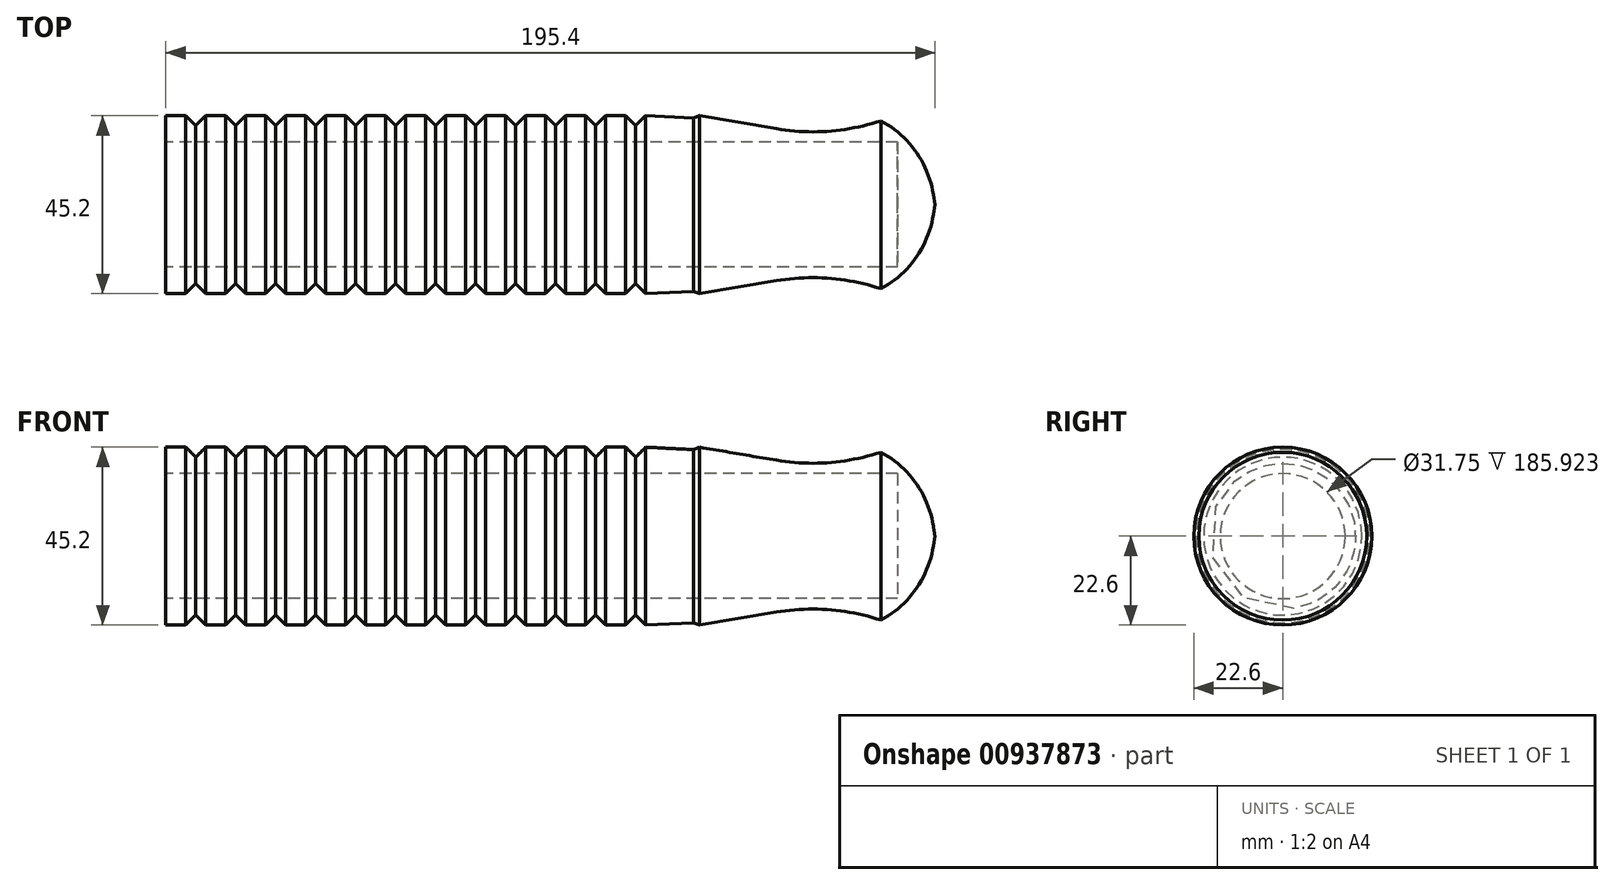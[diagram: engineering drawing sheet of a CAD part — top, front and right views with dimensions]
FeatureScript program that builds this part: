
annotation { "Feature Type Name" : "Feature", "Feature Type Description" : "" }
export const myFeature = defineFeature(function(context is Context, id is Id, definition is map)
    precondition{}
    {
        {
            var Q0;
            Q0=qCreatedBy(makeId("Top.planeOp"),FACE);
            var sketch = newSketch(context, id + "F0", { "sketchPlane" : qUnion([Q0])});
            skLineSegment(sketch, "E0", {"start": v(0, 0) * mm, "end": v(254, 0) * mm});
            skLineSegment(sketch, "E1", {"start": v(254, 0) * mm, "end": v(254, 25.4) * mm});
            skLineSegment(sketch, "E2", {"start": v(254, 25.4) * mm, "end": v(0, 25.4) * mm});
            skLineSegment(sketch, "E3", {"start": v(0, 25.4) * mm, "end": v(0, 0) * mm});
            skLineSegment(sketch, "E4", {"start": v(68.08, 0) * mm, "end": v(68.08, 22.6) * mm});
            skLineSegment(sketch, "E5", {"start": v(187.98, 22.6) * mm, "end": v(187.98, 0) * mm});
            skLineSegment(sketch, "E6", {"start": v(68.08, 22.6) * mm, "end": v(73.16, 22.6) * mm});
            skLineSegment(sketch, "E7", {"start": v(0, 0) * mm, "end": v(0, 15.88) * mm});
            skLineSegment(sketch, "E8", {"start": v(0, 15.88) * mm, "end": v(254, 15.88) * mm});
            skLineSegment(sketch, "E9", {"start": v(75.7, 20.06) * mm, "end": v(73.16, 22.6) * mm});
            skLineSegment(sketch, "E10", {"start": v(75.7, 20.06) * mm, "end": v(75.7, 22.6) * mm});
            skLineSegment(sketch, "E11.MirrorCS", {"start": v(75.7, 20.06) * mm, "end": v(78.24, 22.6) * mm});
            skLineSegment(sketch, "E12.1.0.0", {"start": v(78.24, 22.6) * mm, "end": v(83.32, 22.6) * mm});
            skLineSegment(sketch, "E12.1.0.1", {"start": v(85.86, 20.06) * mm, "end": v(83.32, 22.6) * mm});
            skLineSegment(sketch, "E12.1.0.2", {"start": v(85.86, 20.06) * mm, "end": v(88.4, 22.6) * mm});
            skLineSegment(sketch, "E12.2.0.0", {"start": v(88.4, 22.6) * mm, "end": v(93.48, 22.6) * mm});
            skLineSegment(sketch, "E12.2.0.1", {"start": v(96.02, 20.06) * mm, "end": v(93.48, 22.6) * mm});
            skLineSegment(sketch, "E12.2.0.2", {"start": v(96.02, 20.06) * mm, "end": v(98.56, 22.6) * mm});
            skLineSegment(sketch, "E12.3.0.0", {"start": v(98.56, 22.6) * mm, "end": v(103.64, 22.6) * mm});
            skLineSegment(sketch, "E12.3.0.1", {"start": v(106.18, 20.06) * mm, "end": v(103.64, 22.6) * mm});
            skLineSegment(sketch, "E12.3.0.2", {"start": v(106.18, 20.06) * mm, "end": v(108.72, 22.6) * mm});
            skLineSegment(sketch, "E12.4.0.0", {"start": v(108.72, 22.6) * mm, "end": v(113.8, 22.6) * mm});
            skLineSegment(sketch, "E12.4.0.1", {"start": v(116.34, 20.06) * mm, "end": v(113.8, 22.6) * mm});
            skLineSegment(sketch, "E12.4.0.2", {"start": v(116.34, 20.06) * mm, "end": v(118.88, 22.6) * mm});
            skLineSegment(sketch, "E12.5.0.0", {"start": v(118.88, 22.6) * mm, "end": v(123.96, 22.6) * mm});
            skLineSegment(sketch, "E12.5.0.1", {"start": v(126.5, 20.06) * mm, "end": v(123.96, 22.6) * mm});
            skLineSegment(sketch, "E12.5.0.2", {"start": v(126.5, 20.06) * mm, "end": v(129.04, 22.6) * mm});
            skLineSegment(sketch, "E12.6.0.0", {"start": v(129.04, 22.6) * mm, "end": v(134.12, 22.6) * mm});
            skLineSegment(sketch, "E12.6.0.1", {"start": v(136.66, 20.06) * mm, "end": v(134.12, 22.6) * mm});
            skLineSegment(sketch, "E12.6.0.2", {"start": v(136.66, 20.06) * mm, "end": v(139.2, 22.6) * mm});
            skLineSegment(sketch, "E12.7.0.0", {"start": v(139.2, 22.6) * mm, "end": v(144.28, 22.6) * mm});
            skLineSegment(sketch, "E12.7.0.1", {"start": v(146.82, 20.06) * mm, "end": v(144.28, 22.6) * mm});
            skLineSegment(sketch, "E12.7.0.2", {"start": v(146.82, 20.06) * mm, "end": v(149.36, 22.6) * mm});
            skLineSegment(sketch, "E12.8.0.0", {"start": v(149.36, 22.6) * mm, "end": v(154.44, 22.6) * mm});
            skLineSegment(sketch, "E12.8.0.1", {"start": v(156.98, 20.06) * mm, "end": v(154.44, 22.6) * mm});
            skLineSegment(sketch, "E12.8.0.2", {"start": v(156.98, 20.06) * mm, "end": v(159.52, 22.6) * mm});
            skLineSegment(sketch, "E12.9.0.0", {"start": v(159.52, 22.6) * mm, "end": v(164.6, 22.6) * mm});
            skLineSegment(sketch, "E12.9.0.1", {"start": v(167.14, 20.06) * mm, "end": v(164.6, 22.6) * mm});
            skLineSegment(sketch, "E12.9.0.2", {"start": v(167.14, 20.06) * mm, "end": v(169.68, 22.6) * mm});
            skLineSegment(sketch, "E12.10.0.0", {"start": v(169.68, 22.6) * mm, "end": v(174.76, 22.6) * mm});
            skLineSegment(sketch, "E12.10.0.1", {"start": v(177.3, 20.06) * mm, "end": v(174.76, 22.6) * mm});
            skLineSegment(sketch, "E12.10.0.2", {"start": v(177.3, 20.06) * mm, "end": v(179.84, 22.6) * mm});
            skLineSegment(sketch, "E12.11.0.0", {"start": v(179.84, 22.6) * mm, "end": v(184.92, 22.6) * mm});
            skLineSegment(sketch, "E12.11.0.1", {"start": v(187.46, 20.06) * mm, "end": v(184.92, 22.6) * mm});
            skLineSegment(sketch, "E12.11.0.2", {"start": v(187.46, 20.06) * mm, "end": v(190, 22.6) * mm});
            skLineSegment(sketch, "E12.direction1", {"start": v(68.08, 22.6) * mm, "end": v(78.24, 22.6) * mm, "construction": true});
            skLineSegment(sketch, "E13", {"start": v(190, 22.6) * mm, "end": v(202.16, 22) * mm});
            skLineSegment(sketch, "E14", {"start": v(202.16, 22) * mm, "end": v(203.66, 22.6) * mm});
            skLineSegment(sketch, "E15", {"start": v(203.66, 22.6) * mm, "end": v(223.18, 19.3) * mm});
            skArc(sketch, "E16", {"start": v(223.18, 19.3) * mm, "mid": v(236.59, 18.69) * mm, "end": v(249.75, 21.32) * mm});
            skArc(sketch, "E17", {"start": v(263.08, 2.53) * mm, "mid": v(258.63, 13.5) * mm, "end": v(249.75, 21.32) * mm});
            skLineSegment(sketch, "E18", {"start": v(263.08, 2.53) * mm, "end": v(263.48, 0) * mm});
            skLineSegment(sketch, "E19", {"start": v(263.48, 0) * mm, "end": v(254, 0) * mm});
            skSolve(sketch);
        }
        {
            var Q0;
            {var subQ0=sQuery(id+"F0.wireOp",EDGE,"E6");Q0=makeQuery(id+"F0.imprint","IMPRINT",FACE,{"disambiguationData":[TD([[makeQuery(id+"F0.imprint","IMPRINT",EDGE,{"derivedFrom":subQ0}),-1.0]])]});}
            var Q1;
            {var subQ0=sQuery(id+"F0.wireOp",EDGE,"E13");Q1=makeQuery(id+"F0.imprint","IMPRINT",FACE,{"disambiguationData":[TD([[makeQuery(id+"F0.imprint","IMPRINT",EDGE,{"derivedFrom":subQ0}),-1.0]])]});}
            var Q2;
            {var subQ0=sQuery(id+"F0.wireOp",EDGE,"E18");Q2=makeQuery(id+"F0.imprint","IMPRINT",FACE,{"disambiguationData":[TD([[makeQuery(id+"F0.imprint","IMPRINT",EDGE,{"derivedFrom":subQ0}),-1.0]])]});}
            var Q3;
            Q3=sQuery(id+"F0.wireOp",EDGE,"E0");
            revolve(context, id + "F1", {"surfaceOperationType" : NewSurfaceOperationType.NEW, "entities" : qUnion([Q0, Q1, Q2]), "axis" : qUnion([Q3]), "revolveType" : RevolveType.FULL});
        }
    });
